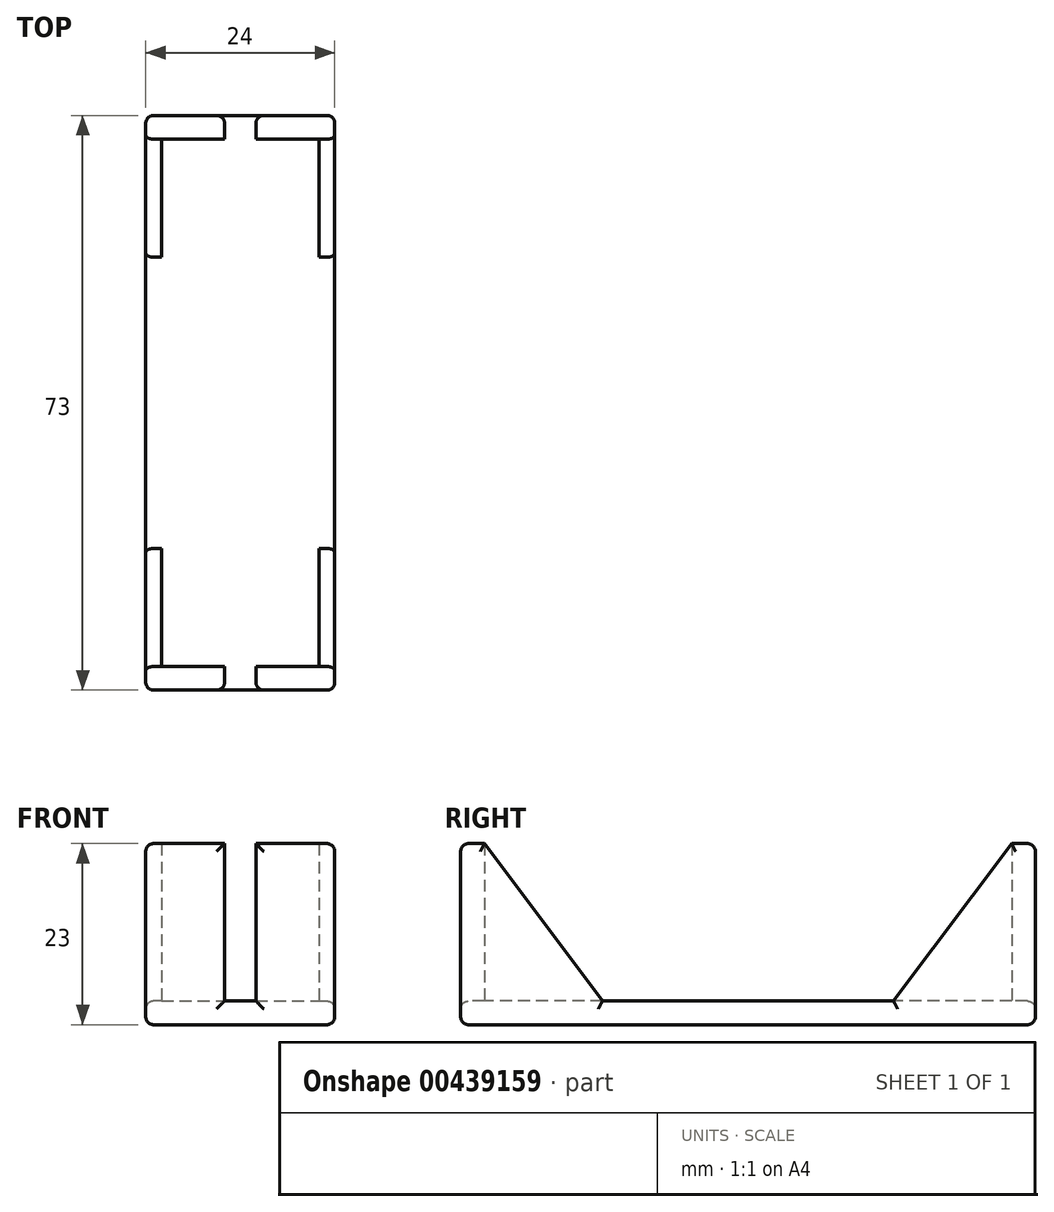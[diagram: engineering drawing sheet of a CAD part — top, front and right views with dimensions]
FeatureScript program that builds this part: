
annotation { "Feature Type Name" : "Feature", "Feature Type Description" : "" }
export const myFeature = defineFeature(function(context is Context, id is Id, definition is map)
    precondition{}
    {
        {
            var Q0;
            Q0=qCreatedBy(makeId("Top.planeOp"),FACE);
            var sketch = newSketch(context, id + "F0", { "sketchPlane" : qUnion([Q0])});
            skLineSegment(sketch, "E0.bottom", {"start": v(2.86, 47.14) * mm, "end": v(26.86, 47.14) * mm});
            skLineSegment(sketch, "E0.top", {"start": v(2.86, -19.86) * mm, "end": v(26.86, -19.86) * mm});
            skLineSegment(sketch, "E0.left", {"start": v(2.86, 47.14) * mm, "end": v(2.86, -19.86) * mm});
            skLineSegment(sketch, "E0.right", {"start": v(26.86, 47.14) * mm, "end": v(26.86, -19.86) * mm});
            skLineSegment(sketch, "E1.top", {"start": v(2.86, -22.86) * mm, "end": v(26.86, -22.86) * mm});
            skLineSegment(sketch, "E1.left", {"start": v(2.86, -19.86) * mm, "end": v(2.86, -22.86) * mm});
            skLineSegment(sketch, "E1.right", {"start": v(26.86, -19.86) * mm, "end": v(26.86, -22.86) * mm});
            skLineSegment(sketch, "E2.top", {"start": v(2.86, 50.14) * mm, "end": v(26.86, 50.14) * mm});
            skLineSegment(sketch, "E2.left", {"start": v(2.86, 47.14) * mm, "end": v(2.86, 50.14) * mm});
            skLineSegment(sketch, "E2.right", {"start": v(26.86, 47.14) * mm, "end": v(26.86, 50.14) * mm});
            skLineSegment(sketch, "E3", {"start": v(12.86, 47.14) * mm, "end": v(12.86, 50.14) * mm});
            skPoint(sketch, "E3.endSnap0", {"position": v(14.86, 50.14) * mm});
            skLineSegment(sketch, "E4", {"start": v(16.86, 50.14) * mm, "end": v(16.86, 47.14) * mm});
            skLineSegment(sketch, "E5", {"start": v(12.86, -19.86) * mm, "end": v(12.86, -22.86) * mm});
            skLineSegment(sketch, "E6", {"start": v(16.86, -19.86) * mm, "end": v(16.86, -22.86) * mm});
            skSolve(sketch);
        }
        {
            var Q0;
            {var subQ0=sQuery(id+"F0.wireOp",EDGE,"E2.right");Q0=makeQuery(id+"F0.imprint","IMPRINT",FACE,{"disambiguationData":[TD([[makeQuery(id+"F0.imprint","IMPRINT",EDGE,{"derivedFrom":subQ0}),1.0]])]});}
            var Q1;
            {var subQ0=sQuery(id+"F0.wireOp",EDGE,"E2.left");Q1=makeQuery(id+"F0.imprint","IMPRINT",FACE,{"disambiguationData":[TD([[makeQuery(id+"F0.imprint","IMPRINT",EDGE,{"derivedFrom":subQ0}),-1.0]])]});}
            var Q2;
            {var subQ0=sQuery(id+"F0.wireOp",EDGE,"E1.left");Q2=makeQuery(id+"F0.imprint","IMPRINT",FACE,{"disambiguationData":[TD([[makeQuery(id+"F0.imprint","IMPRINT",EDGE,{"derivedFrom":subQ0}),1.0]])]});}
            var Q3;
            {var subQ0=sQuery(id+"F0.wireOp",EDGE,"E1.right");Q3=makeQuery(id+"F0.imprint","IMPRINT",FACE,{"disambiguationData":[TD([[makeQuery(id+"F0.imprint","IMPRINT",EDGE,{"derivedFrom":subQ0}),-1.0]])]});}
            extrude(context, id + "F1", {"entities" : qUnion([Q0, Q1, Q2, Q3]), "depth" : 23 * mm});
        }
        {
            var Q0;
            {var subQ3=sQuery(id+"F0.wireOp",EDGE,"E0.left");Q0=makeQuery(id+"F0.imprint","IMPRINT",FACE,{"disambiguationData":[TD([[makeQuery(id+"F0.imprint","IMPRINT",EDGE,{"derivedFrom":subQ3}),1.0]])]});}
            var Q1;
            {var subQ0=sQuery(id+"F0.wireOp",EDGE,"E5");Q1=makeQuery(id+"F0.imprint","IMPRINT",FACE,{"disambiguationData":[TD([[makeQuery(id+"F0.imprint","IMPRINT",EDGE,{"derivedFrom":subQ0}),1.0]])]});}
            var Q2;
            {var subQ0=sQuery(id+"F0.wireOp",EDGE,"E3");Q2=makeQuery(id+"F0.imprint","IMPRINT",FACE,{"disambiguationData":[TD([[makeQuery(id+"F0.imprint","IMPRINT",EDGE,{"derivedFrom":subQ0}),-1.0]])]});}
            extrude(context, id + "F2", {"entities" : qUnion([Q0, Q1, Q2]), "operationType" : NewBodyOperationType.ADD, "depth" : 3 * mm});
        }
        {
            var Q0;
            Q0=makeQuery(id+"F2.boolean.opBoolean","MERGE",FACE,{"derivedFrom":[makeQuery(id+"F1.opExtrude","SWEPT_FACE",FACE,{"disambiguationData":[OSD([sQuery(id+"F0.wireOp",EDGE,"E1.left")])]}),makeQuery(id+"F1.opExtrude","SWEPT_FACE",FACE,{"disambiguationData":[OSD([sQuery(id+"F0.wireOp",EDGE,"E2.left")])]}),makeQuery(id+"F2.opExtrude","SWEPT_FACE",FACE,{"disambiguationData":[OSD([sQuery(id+"F0.wireOp",EDGE,"E0.left")])]})]});
            var sketch = newSketch(context, id + "F3", { "sketchPlane" : qUnion([Q0])});
            skLineSegment(sketch, "E7", {"start": v(-47.14, 23) * mm, "end": v(-32.14, 3) * mm});
            skLineSegment(sketch, "E8", {"start": v(19.86, 23) * mm, "end": v(4.86, 3) * mm});
            skSolve(sketch);
        }
        {
            var Q0;
            {var subQ0=sQuery(id+"F3.wireOp",EDGE,"E8");Q0=makeQuery(id+"F3.imprint","IMPRINT",FACE,{"disambiguationData":[TD([[makeQuery(id+"F3.imprint","IMPRINT",EDGE,{"derivedFrom":subQ0}),1.0]])]});}
            var Q1;
            {var subQ0=sQuery(id+"F3.wireOp",EDGE,"E7");Q1=makeQuery(id+"F3.imprint","IMPRINT",FACE,{"disambiguationData":[TD([[makeQuery(id+"F3.imprint","IMPRINT",EDGE,{"derivedFrom":subQ0}),-1.0]])]});}
            extrude(context, id + "F4", {"entities" : qUnion([Q0, Q1]), "operationType" : NewBodyOperationType.ADD, "oppositeDirection" : true, "depth" : 2 * mm});
        }
        {
            var Q0;
            Q0=makeQuery(id+"F2.boolean.opBoolean","MERGE",FACE,{"derivedFrom":[makeQuery(id+"F1.opExtrude","SWEPT_FACE",FACE,{"disambiguationData":[OSD([sQuery(id+"F0.wireOp",EDGE,"E1.right")])]}),makeQuery(id+"F1.opExtrude","SWEPT_FACE",FACE,{"disambiguationData":[OSD([sQuery(id+"F0.wireOp",EDGE,"E2.right")])]}),makeQuery(id+"F2.opExtrude","SWEPT_FACE",FACE,{"disambiguationData":[OSD([sQuery(id+"F0.wireOp",EDGE,"E0.right")])]})]});
            var sketch = newSketch(context, id + "F5", { "sketchPlane" : qUnion([Q0])});
            skLineSegment(sketch, "E9", {"start": v(-19.86, 23) * mm, "end": v(-4.86, 3) * mm});
            skLineSegment(sketch, "E10", {"start": v(47.14, 23) * mm, "end": v(32.14, 3) * mm});
            skSolve(sketch);
        }
        {
            var Q0;
            {var subQ0=sQuery(id+"F5.wireOp",EDGE,"E10");Q0=makeQuery(id+"F5.imprint","IMPRINT",FACE,{"disambiguationData":[TD([[makeQuery(id+"F5.imprint","IMPRINT",EDGE,{"derivedFrom":subQ0}),1.0]])]});}
            var Q1;
            {var subQ0=sQuery(id+"F5.wireOp",EDGE,"E9");Q1=makeQuery(id+"F5.imprint","IMPRINT",FACE,{"disambiguationData":[TD([[makeQuery(id+"F5.imprint","IMPRINT",EDGE,{"derivedFrom":subQ0}),-1.0]])]});}
            extrude(context, id + "F6", {"entities" : qUnion([Q0, Q1]), "operationType" : NewBodyOperationType.ADD, "oppositeDirection" : true, "depth" : 2 * mm});
        }
        {
            var Q0;
            {var subQ0=sQuery(id+"F0.wireOp",EDGE,"E6");var subQ1=sQuery(id+"F0.wireOp",EDGE,"E5");var subQ2=sQuery(id+"F0.wireOp",EDGE,"E4");var subQ3=sQuery(id+"F0.wireOp",EDGE,"E3");var subQ4=sQuery(id+"F0.wireOp",EDGE,"E2.top");var subQ5=sQuery(id+"F0.wireOp",EDGE,"E0.bottom");var subQ6=sQuery(id+"F0.wireOp",EDGE,"E1.top");var subQ7=sQuery(id+"F0.wireOp",EDGE,"E0.top");Q0=makeQuery(id+"F2.boolean.opBoolean","MERGE",FACE,{"derivedFrom":[makeQuery(id+"F1.opExtrude","CAP_FACE",FACE,{"disambiguationData":[OSD([subQ7,subQ6,sQuery(id+"F0.wireOp",EDGE,"E1.left"),subQ1])],"isStart":true}),makeQuery(id+"F1.opExtrude","CAP_FACE",FACE,{"disambiguationData":[OSD([subQ7,subQ6,sQuery(id+"F0.wireOp",EDGE,"E1.right"),subQ0])],"isStart":true}),makeQuery(id+"F1.opExtrude","CAP_FACE",FACE,{"disambiguationData":[OSD([subQ5,subQ4,sQuery(id+"F0.wireOp",EDGE,"E2.left"),subQ3])],"isStart":true}),makeQuery(id+"F1.opExtrude","CAP_FACE",FACE,{"disambiguationData":[OSD([subQ5,subQ4,sQuery(id+"F0.wireOp",EDGE,"E2.right"),subQ2])],"isStart":true}),makeQuery(id+"F2.opExtrude","CAP_FACE",FACE,{"disambiguationData":[OSD([sQuery(id+"F0.wireOp",EDGE,"E0.left"),sQuery(id+"F0.wireOp",EDGE,"E0.right"),subQ7,subQ6,subQ5,subQ4,subQ3,subQ2,subQ1,subQ0])],"isStart":true})]});}
            var Q1;
            {var subQ0=sQuery(id+"F0.wireOp",EDGE,"E1.top");Q1=makeQuery(id+"F2.boolean.opBoolean","MERGE",FACE,{"derivedFrom":[makeQuery(id+"F1.opExtrude","SWEPT_FACE",FACE,{"disambiguationData":[OSD([subQ0]),TDD([makeQuery(id+"F0.imprint","IMPRINT",EDGE,{"disambiguationData":[TD([[makeQuery(id+"F0.imprint","INTERSECT",VERTEX,{"derivedFrom":[subQ0,sQuery(id+"F0.wireOp",EDGE,"E1.left")]}),-1.0]])],"derivedFrom":subQ0})])]}),makeQuery(id+"F1.opExtrude","SWEPT_FACE",FACE,{"disambiguationData":[OSD([subQ0]),TDD([makeQuery(id+"F0.imprint","IMPRINT",EDGE,{"disambiguationData":[TD([[makeQuery(id+"F0.imprint","INTERSECT",VERTEX,{"derivedFrom":[subQ0,sQuery(id+"F0.wireOp",EDGE,"E1.right")]}),1.0]])],"derivedFrom":subQ0})])]}),makeQuery(id+"F2.opExtrude","SWEPT_FACE",FACE,{"disambiguationData":[OSD([subQ0])]})]});}
            var Q2;
            {var subQ0=sQuery(id+"F0.wireOp",EDGE,"E2.top");Q2=makeQuery(id+"F2.boolean.opBoolean","MERGE",FACE,{"derivedFrom":[makeQuery(id+"F1.opExtrude","SWEPT_FACE",FACE,{"disambiguationData":[OSD([subQ0]),TDD([makeQuery(id+"F0.imprint","IMPRINT",EDGE,{"disambiguationData":[TD([[makeQuery(id+"F0.imprint","INTERSECT",VERTEX,{"derivedFrom":[subQ0,sQuery(id+"F0.wireOp",EDGE,"E2.left")]}),-1.0]])],"derivedFrom":subQ0})])]}),makeQuery(id+"F1.opExtrude","SWEPT_FACE",FACE,{"disambiguationData":[OSD([subQ0]),TDD([makeQuery(id+"F0.imprint","IMPRINT",EDGE,{"disambiguationData":[TD([[makeQuery(id+"F0.imprint","INTERSECT",VERTEX,{"derivedFrom":[subQ0,sQuery(id+"F0.wireOp",EDGE,"E2.right")]}),1.0]])],"derivedFrom":subQ0})])]}),makeQuery(id+"F2.opExtrude","SWEPT_FACE",FACE,{"disambiguationData":[OSD([subQ0])]})]});}
            var Q3;
            {var subQ0=sQuery(id+"F0.wireOp",EDGE,"E1.left");var subQ1=sQuery(id+"F0.wireOp",EDGE,"E0.left");var subQ2=sQuery(id+"F0.wireOp",EDGE,"E2.left");Q3=makeQuery(id+"F4.boolean.opBoolean","MERGE",FACE,{"derivedFrom":[makeQuery(id+"F2.boolean.opBoolean","MERGE",FACE,{"derivedFrom":[makeQuery(id+"F1.opExtrude","SWEPT_FACE",FACE,{"disambiguationData":[OSD([subQ0])]}),makeQuery(id+"F1.opExtrude","SWEPT_FACE",FACE,{"disambiguationData":[OSD([subQ2])]}),makeQuery(id+"F2.opExtrude","SWEPT_FACE",FACE,{"disambiguationData":[OSD([subQ1])]})]}),makeQuery(id+"F4.opExtrude","CAP_FACE",FACE,{"disambiguationData":[OSD([subQ1,sQuery(id+"F0.wireOp",EDGE,"E0.bottom"),subQ2,sQuery(id+"F3.wireOp",EDGE,"E7")])],"isStart":true}),makeQuery(id+"F4.opExtrude","CAP_FACE",FACE,{"disambiguationData":[OSD([subQ1,sQuery(id+"F0.wireOp",EDGE,"E0.top"),subQ0,sQuery(id+"F3.wireOp",EDGE,"E8")])],"isStart":true})]});}
            var Q4;
            {var subQ0=sQuery(id+"F0.wireOp",EDGE,"E2.right");var subQ1=sQuery(id+"F0.wireOp",EDGE,"E0.right");var subQ2=sQuery(id+"F0.wireOp",EDGE,"E1.right");Q4=makeQuery(id+"F6.boolean.opBoolean","MERGE",FACE,{"derivedFrom":[makeQuery(id+"F2.boolean.opBoolean","MERGE",FACE,{"derivedFrom":[makeQuery(id+"F1.opExtrude","SWEPT_FACE",FACE,{"disambiguationData":[OSD([subQ2])]}),makeQuery(id+"F1.opExtrude","SWEPT_FACE",FACE,{"disambiguationData":[OSD([subQ0])]}),makeQuery(id+"F2.opExtrude","SWEPT_FACE",FACE,{"disambiguationData":[OSD([subQ1])]})]}),makeQuery(id+"F6.opExtrude","CAP_FACE",FACE,{"disambiguationData":[OSD([subQ1,sQuery(id+"F0.wireOp",EDGE,"E0.top"),subQ2,sQuery(id+"F5.wireOp",EDGE,"E9")])],"isStart":true}),makeQuery(id+"F6.opExtrude","CAP_FACE",FACE,{"disambiguationData":[OSD([subQ1,sQuery(id+"F0.wireOp",EDGE,"E0.bottom"),subQ0,sQuery(id+"F5.wireOp",EDGE,"E10")])],"isStart":true})]});}
            fillet(context, id + "F7", {"entities" : qUnion([Q0, Q1, Q2, Q3, Q4]), "radius" : 1 * mm, "tangentPropagation" : true, "allowEdgeOverflow" : false});
        }
    });
